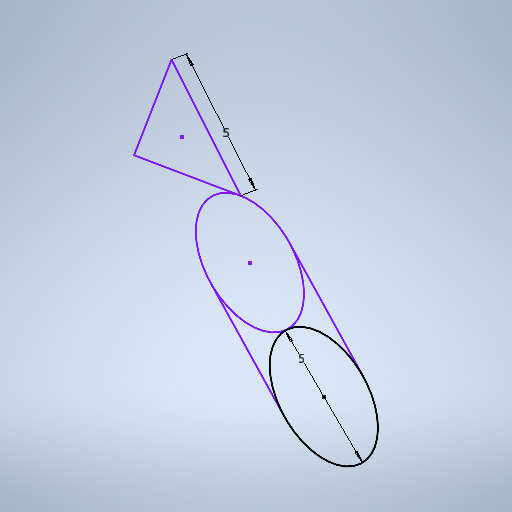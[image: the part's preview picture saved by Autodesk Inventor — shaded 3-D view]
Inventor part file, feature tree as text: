
AUTODESK INVENTOR PART (.ipt)
format: ipt  version: 2025.2 (Build 292293000, 293)  size: 261,632 bytes
history: native  units: mm
features: sketch x1
ambient origin geometry x8: Origin, YZ Plane, XZ Plane, XY Plane, X Axis, Y Axis, Z Axis, Center Point
feature tree (1):
  sketch  "Esboço1"  dims[d0=5.0mm d2=5.0mm]
